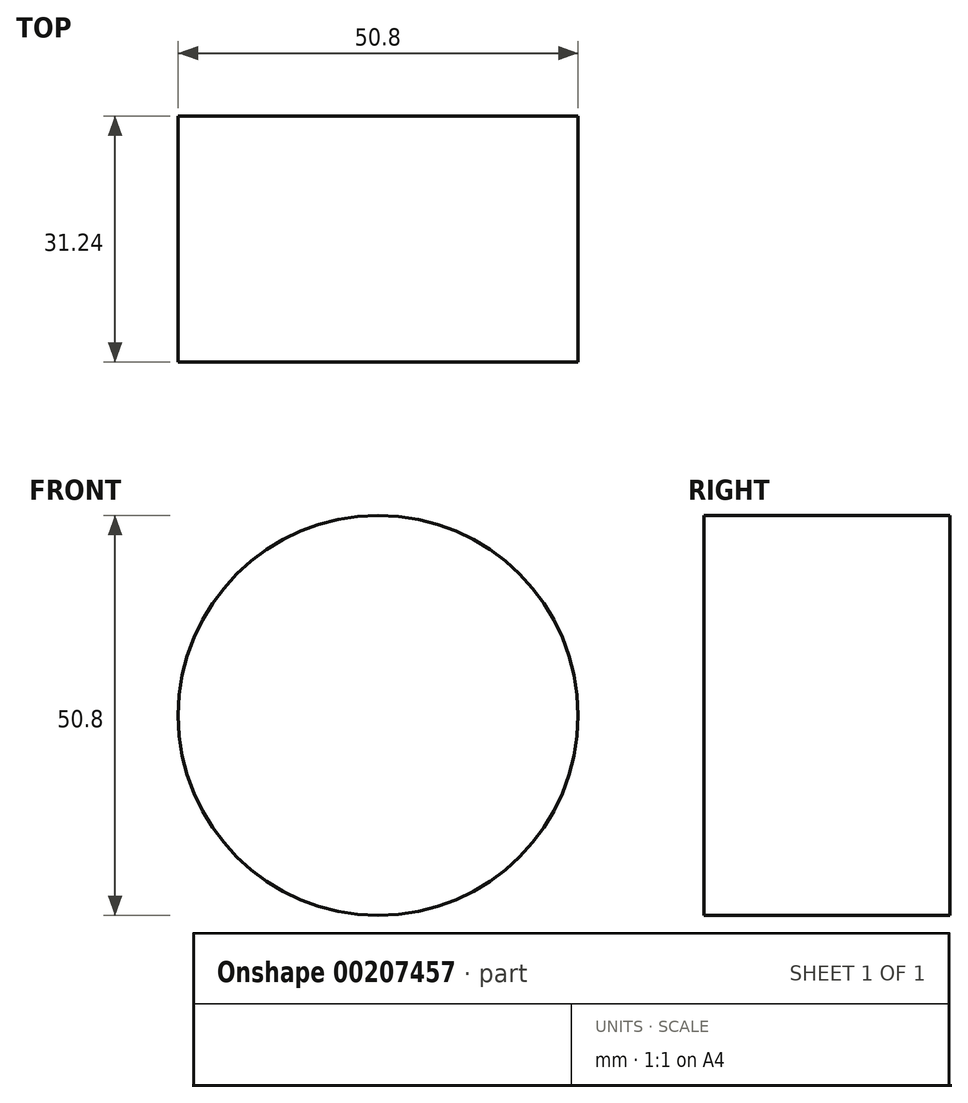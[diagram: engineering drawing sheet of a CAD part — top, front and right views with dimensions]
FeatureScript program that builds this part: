
annotation { "Feature Type Name" : "Feature", "Feature Type Description" : "" }
export const myFeature = defineFeature(function(context is Context, id is Id, definition is map)
    precondition{}
    {
        {
            var Q0;
            Q0=qCreatedBy(makeId("Front.planeOp"),FACE);
            var sketch = newSketch(context, id + "F0", { "sketchPlane" : qUnion([Q0])});
            skCircle(sketch, "E0", {"center": v(0, 0) * mm, "radius": 25.4 * mm});
            skSolve(sketch);
        }
        {
            var Q0;
            Q0 = qSketchRegion(id + "F0", true);
            extrude(context, id + "F1", {"entities" : qUnion([Q0]), "depth" : 31.24 * mm});
        }
    });
